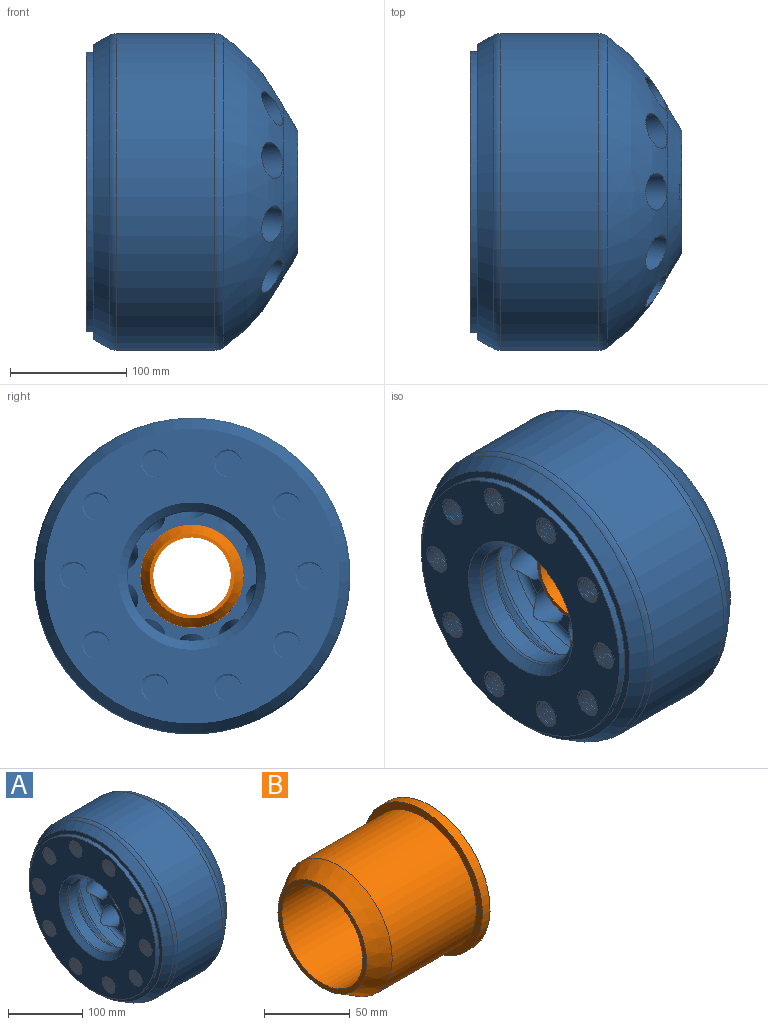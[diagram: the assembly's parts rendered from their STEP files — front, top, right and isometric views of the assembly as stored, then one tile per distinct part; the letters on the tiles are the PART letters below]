
ASSEMBLY  parts=2 mates=1
PART A: 256 faces, bbox 209.3x320.9x320.9 mm
  f0: cone r=52.39mm half-angle=59.3deg, axis (-1,0,0), area 9491.2mm2, adj f3,f15,f253,f254,f255
  f1: cylinder r=50.8mm len=101.6mm, axis (1,0,0), area 11189.3mm2, adj f2,f15,f253,f254
  f2: plane 114.3x114.3mm, normal (-1,0,0), area 2081.3mm2, adj f1,f23,f253,f254,f255
  f3: sphere r=165.1mm, area 45323.7mm2, adj f0,f16,f33,f34,f35,f36,f37,f38
  f4: cylinder r=79.38mm len=158.75mm, axis (1,0,0), area 6975.3mm2, adj f5,f6,f7,f8,f9,f10,f11,f12
  f5: torus R=73.03mm, axis (1,0,0), area 259.8mm2, adj f4,f26,f41,f42
  f6: torus R=73.03mm, axis (1,0,0), area 259.8mm2, adj f4,f26,f33,f42
  f7: torus R=73.03mm, axis (1,0,0), area 18306.5mm2, adj f4,f26,f40,f41
  f8: torus R=73.03mm, axis (1,0,0), area 0mm2, adj f4,f26,f39,f40
  f9: torus R=73.03mm, axis (1,0,0), area 494mm2, adj f4,f26,f38,f39
  f10: torus R=73.03mm, axis (1,0,0), area 259.8mm2, adj f4,f26,f37,f38
  f11: torus R=73.03mm, axis (1,0,0), area 259.8mm2, adj f4,f26,f36,f37
  f12: torus R=73.03mm, axis (1,0,0), area 18306.5mm2, adj f4,f26,f35,f36
  f13: torus R=73.03mm, axis (1,0,0), area 0mm2, adj f4,f26,f34,f35
  f14: torus R=73.03mm, axis (1,0,0), area 259.8mm2, adj f4,f26,f33,f34
  f15: plane 104.78x104.39mm, normal (1,0,0), area 494.4mm2, adj f0,f1,f253,f254
  f16: torus R=123.83mm, axis (-1,0,0), area 6740.3mm2, adj f3,f17
  f17: cylinder r=136.53mm len=273.05mm, axis (-1,0,0), area 72757.5mm2, adj f16,f18
  f18: torus R=123.83mm, axis (-1,0,0), area 5680.3mm2, adj f17,f19
  f19: cone r=127mm half-angle=30deg, axis (1,0,0), area 12870.4mm2, adj f18,f20
  f20: plane 254x254mm, normal (-1,0,0), area 4940.4mm2, adj f19,f21
  f21: cylinder r=120.65mm len=241.3mm, axis (-1,0,0), area 4813.7mm2, adj f20,f22
  f22: plane 242.26x242.26mm, normal (-1,0,0), area 28619.3mm2, adj f21,f32,f43,f44,f48,f61,f64,f65
  f23: cylinder r=57.15mm len=114.3mm, axis (1,0,0), area 2280.2mm2, adj f2,f24
  f24: plane 114.3x114.3mm, normal (1,0,0), area 4053.7mm2, adj f23,f25
  f25: cylinder r=44.45mm len=88.9mm, axis (1,0,0), area 18178.1mm2, adj f24,f26
  f26: plane 171.45x168.36mm, normal (-1,0,0), area 4413.4mm2, adj f5,f6,f7,f8,f9,f10,f11,f12
  f27: torus R=73.03mm, axis (1,0,0), area 2467.5mm2, adj f4,f28
  f28: cone r=56.49mm half-angle=45deg, axis (1,0,0), area 12516.5mm2, adj f27,f29
  f29: torus R=58.74mm, axis (1,0,0), area 875.5mm2, adj f28,f30
  f30: cylinder r=55.56mm len=111.13mm, axis (1,0,0), area 5732.3mm2, adj f29,f31
  f31: torus R=58.74mm, axis (1,0,0), area 875.5mm2, adj f30,f32
  f32: cone r=63.5mm half-angle=45deg, axis (-1,0,0), area 3735.8mm2, adj f22,f31
  f33: cylinder r=15.88mm len=105.94mm, axis (-0.97,0,-0.26), area 9094.1mm2, adj f3,f4,f6,f14,f26
  f34: cylinder r=15.88mm len=101.5mm, axis (-0.97,0.15,-0.21), area 8854.5mm2, adj f3,f4,f13,f14,f26
  f35: cylinder r=15.88mm len=105.94mm, axis (-0.97,0.25,-0.08), area 9081.9mm2, adj f3,f4,f12,f13,f26
  f36: cylinder r=15.88mm len=105.94mm, axis (-0.97,0.25,0.08), area 9082mm2, adj f3,f4,f11,f12,f26
  f37: cylinder r=15.88mm len=101.5mm, axis (-0.97,0.15,0.21), area 8835.7mm2, adj f3,f4,f10,f11,f26
  f38: cylinder r=15.88mm len=105.94mm, axis (-0.97,0,0.26), area 9106.3mm2, adj f3,f4,f9,f10,f26
  f39: cylinder r=15.88mm len=98.67mm, axis (-0.97,-0.15,0.21), area 8845.8mm2, adj f3,f4,f8,f9,f26
  f40: cylinder r=15.88mm len=105.94mm, axis (-0.97,-0.25,0.08), area 9052mm2, adj f3,f4,f7,f8,f26
  f41: cylinder r=15.88mm len=102.22mm, axis (-0.97,-0.25,-0.08), area 8973.2mm2, adj f3,f4,f5,f7,f26
  f42: cylinder r=15.88mm len=100.03mm, axis (-0.97,-0.15,-0.21), area 8769.5mm2, adj f3,f4,f5,f6,f26
  f43: bspline ~37.5x29.63mm, area 1693.9mm2, adj f22,f46,f48,f50,f51,f52,f53,f54
  f44: bspline ~36.45x29.63mm, area 1629.6mm2, adj f22,f45,f48,f51,f52,f53,f54,f55
  f45: bspline ~24.97x24.28mm, area 78.5mm2, adj f44,f47,f49,f50,f62
  f46: bspline ~24.86x24.06mm, area 78.4mm2, adj f43,f47,f49,f62
  f47: bspline ~25.26x24.57mm, area 35mm2, adj f45,f46,f48,f62
  f48: bspline ~36.38x29.97mm, area 413.9mm2, adj f22,f43,f44,f47
  f49: cylinder r=11.11mm len=22.23mm, axis (-1,0,0), area 1251.3mm2, adj f45,f46,f50,f62,f63
  f50: cylinder r=11.11mm len=22.23mm, axis (-1,0,0), area 87.5mm2, adj f43,f45,f49,f51
  f51: cylinder r=11.11mm len=22.23mm, axis (-1,0,0), area 55.5mm2, adj f43,f44,f50,f52
  f52: cylinder r=11.11mm len=22.23mm, axis (-1,0,0), area 55.5mm2, adj f43,f44,f51,f53
  f53: cylinder r=11.11mm len=22.23mm, axis (-1,0,0), area 55.4mm2, adj f43,f44,f52,f54
  f54: cylinder r=11.11mm len=22.23mm, axis (-1,0,0), area 55.4mm2, adj f43,f44,f53,f55
  f55: cylinder r=11.11mm len=22.23mm, axis (-1,0,0), area 55.3mm2, adj f43,f44,f54,f56
  f56: cylinder r=11.11mm len=22.23mm, axis (-1,0,0), area 55.4mm2, adj f43,f44,f55,f57
  f57: cylinder r=11.11mm len=22.23mm, axis (-1,0,0), area 55.5mm2, adj f43,f44,f56,f58
  f58: cylinder r=11.11mm len=22.23mm, axis (-1,0,0), area 55.4mm2, adj f43,f44,f57,f59
  f59: cylinder r=11.11mm len=22.23mm, axis (-1,0,0), area 55.5mm2, adj f43,f44,f58,f60
  f60: cylinder r=11.11mm len=22.23mm, axis (-1,0,0), area 55.4mm2, adj f43,f44,f59,f61
  f61: cylinder r=11.11mm len=22.23mm, axis (-1,0,0), area 34.6mm2, adj f22,f43,f44,f60
  f62: plane 0.56x0.24mm, normal (-0.01,1,0), area 0.1mm2, adj f45,f46,f47,f49
  f63: plane 22.23x22.23mm, normal (-1,0,0), area 387.9mm2, adj f49
  f64: bspline ~37.5x29.63mm, area 1693.9mm2, adj f22,f67,f69,f71,f72,f73,f74,f75
  f65: bspline ~36.45x29.63mm, area 1629.6mm2, adj f22,f66,f69,f72,f73,f74,f75,f76
  f66: bspline ~24.97x24.28mm, area 78.5mm2, adj f65,f68,f70,f71,f83
  f67: bspline ~24.97x24.28mm, area 78.4mm2, adj f64,f68,f70,f83
  f68: bspline ~25.26x24.57mm, area 35mm2, adj f66,f67,f69,f83
  f69: bspline ~36.38x29.97mm, area 413.9mm2, adj f22,f64,f65,f68
  f70: cylinder r=11.11mm len=22.23mm, axis (-1,0,0), area 1251.3mm2, adj f66,f67,f71,f83,f84
  f71: cylinder r=11.11mm len=22.23mm, axis (-1,0,0), area 87.5mm2, adj f64,f66,f70,f72
  f72: cylinder r=11.11mm len=22.23mm, axis (-1,0,0), area 55.5mm2, adj f64,f65,f71,f73
  f73: cylinder r=11.11mm len=22.23mm, axis (-1,0,0), area 55.5mm2, adj f64,f65,f72,f74
  f74: cylinder r=11.11mm len=22.23mm, axis (-1,0,0), area 55.4mm2, adj f64,f65,f73,f75
  f75: cylinder r=11.11mm len=22.23mm, axis (-1,0,0), area 55.4mm2, adj f64,f65,f74,f76
  f76: cylinder r=11.11mm len=22.23mm, axis (-1,0,0), area 55.3mm2, adj f64,f65,f75,f77
  f77: cylinder r=11.11mm len=22.23mm, axis (-1,0,0), area 55.4mm2, adj f64,f65,f76,f78
  f78: cylinder r=11.11mm len=22.23mm, axis (-1,0,0), area 55.5mm2, adj f64,f65,f77,f79
  f79: cylinder r=11.11mm len=22.23mm, axis (-1,0,0), area 55.4mm2, adj f64,f65,f78,f80
  f80: cylinder r=11.11mm len=22.23mm, axis (-1,0,0), area 55.5mm2, adj f64,f65,f79,f81
  f81: cylinder r=11.11mm len=22.23mm, axis (-1,0,0), area 55.4mm2, adj f64,f65,f80,f82
  f82: cylinder r=11.11mm len=22.23mm, axis (-1,0,0), area 34.6mm2, adj f22,f64,f65,f81
  f83: plane 0.56x0.24mm, normal (-0.01,1,0), area 0.1mm2, adj f66,f67,f68,f70
  f84: plane 22.23x22.23mm, normal (-1,0,0), area 387.9mm2, adj f70
  f85: bspline ~37.5x29.63mm, area 1693.9mm2, adj f22,f88,f90,f92,f93,f94,f95,f96
  f86: bspline ~36.45x29.63mm, area 1629.6mm2, adj f22,f87,f90,f93,f94,f95,f96,f97
  f87: bspline ~24.97x24.28mm, area 78.5mm2, adj f86,f89,f91,f92,f104
  f88: bspline ~24.97x24.28mm, area 78.4mm2, adj f85,f89,f91,f104
  f89: bspline ~25.26x24.57mm, area 35mm2, adj f87,f88,f90,f104
  f90: bspline ~36.38x29.97mm, area 413.9mm2, adj f22,f85,f86,f89
  f91: cylinder r=11.11mm len=22.23mm, axis (-1,0,0), area 1251.3mm2, adj f87,f88,f92,f104,f105
  f92: cylinder r=11.11mm len=22.23mm, axis (-1,0,0), area 87.5mm2, adj f85,f87,f91,f93
  f93: cylinder r=11.11mm len=22.23mm, axis (-1,0,0), area 55.5mm2, adj f85,f86,f92,f94
  f94: cylinder r=11.11mm len=22.23mm, axis (-1,0,0), area 55.5mm2, adj f85,f86,f93,f95
  f95: cylinder r=11.11mm len=22.23mm, axis (-1,0,0), area 55.4mm2, adj f85,f86,f94,f96
  f96: cylinder r=11.11mm len=22.23mm, axis (-1,0,0), area 55.4mm2, adj f85,f86,f95,f97
  f97: cylinder r=11.11mm len=22.23mm, axis (-1,0,0), area 55.3mm2, adj f85,f86,f96,f98
  f98: cylinder r=11.11mm len=22.23mm, axis (-1,0,0), area 55.4mm2, adj f85,f86,f97,f99
  f99: cylinder r=11.11mm len=22.23mm, axis (-1,0,0), area 55.5mm2, adj f85,f86,f98,f100
  f100: cylinder r=11.11mm len=22.23mm, axis (-1,0,0), area 55.4mm2, adj f85,f86,f99,f101
  f101: cylinder r=11.11mm len=22.23mm, axis (-1,0,0), area 55.5mm2, adj f85,f86,f100,f102
  f102: cylinder r=11.11mm len=22.23mm, axis (-1,0,0), area 55.4mm2, adj f85,f86,f101,f103
  f103: cylinder r=11.11mm len=22.23mm, axis (-1,0,0), area 34.6mm2, adj f22,f85,f86,f102
  f104: plane 0.56x0.24mm, normal (-0.01,1,0), area 0.1mm2, adj f87,f88,f89,f91
  f105: plane 22.23x22.23mm, normal (-1,0,0), area 387.9mm2, adj f91
  f106: bspline ~37.5x29.63mm, area 1693.9mm2, adj f22,f109,f111,f113,f114,f115,f116,f117
  f107: bspline ~36.45x29.63mm, area 1629.6mm2, adj f22,f108,f111,f114,f115,f116,f117,f118
  f108: bspline ~24.86x24.06mm, area 78.5mm2, adj f107,f110,f112,f113,f125
  f109: bspline ~24.97x24.28mm, area 78.4mm2, adj f106,f110,f112,f125
  f110: bspline ~25.26x24.57mm, area 35mm2, adj f108,f109,f111,f125
  f111: bspline ~36.38x29.97mm, area 413.9mm2, adj f22,f106,f107,f110
  f112: cylinder r=11.11mm len=22.23mm, axis (-1,0,0), area 1251.3mm2, adj f108,f109,f113,f125,f126
  f113: cylinder r=11.11mm len=22.23mm, axis (-1,0,0), area 87.5mm2, adj f106,f108,f112,f114
  f114: cylinder r=11.11mm len=22.23mm, axis (-1,0,0), area 55.5mm2, adj f106,f107,f113,f115
  f115: cylinder r=11.11mm len=22.23mm, axis (-1,0,0), area 55.5mm2, adj f106,f107,f114,f116
  f116: cylinder r=11.11mm len=22.23mm, axis (-1,0,0), area 55.4mm2, adj f106,f107,f115,f117
  f117: cylinder r=11.11mm len=22.23mm, axis (-1,0,0), area 55.4mm2, adj f106,f107,f116,f118
  f118: cylinder r=11.11mm len=22.23mm, axis (-1,0,0), area 55.3mm2, adj f106,f107,f117,f119
  f119: cylinder r=11.11mm len=22.23mm, axis (-1,0,0), area 55.4mm2, adj f106,f107,f118,f120
  f120: cylinder r=11.11mm len=22.23mm, axis (-1,0,0), area 55.5mm2, adj f106,f107,f119,f121
  f121: cylinder r=11.11mm len=22.23mm, axis (-1,0,0), area 55.4mm2, adj f106,f107,f120,f122
  f122: cylinder r=11.11mm len=22.23mm, axis (-1,0,0), area 55.5mm2, adj f106,f107,f121,f123
  f123: cylinder r=11.11mm len=22.23mm, axis (-1,0,0), area 55.4mm2, adj f106,f107,f122,f124
  f124: cylinder r=11.11mm len=22.23mm, axis (-1,0,0), area 34.6mm2, adj f22,f106,f107,f123
  f125: plane 0.56x0.24mm, normal (-0.01,1,0), area 0.1mm2, adj f108,f109,f110,f112
  f126: plane 22.23x22.23mm, normal (-1,0,0), area 387.9mm2, adj f112
  f127: bspline ~37.5x29.63mm, area 1693.9mm2, adj f22,f130,f132,f134,f135,f136,f137,f138
  f128: bspline ~36.45x29.63mm, area 1629.6mm2, adj f22,f129,f132,f135,f136,f137,f138,f139
  f129: bspline ~24.86x24.06mm, area 78.5mm2, adj f128,f131,f133,f134,f146
  f130: bspline ~24.97x24.28mm, area 78.4mm2, adj f127,f131,f133,f146
  f131: bspline ~25.26x24.57mm, area 35mm2, adj f129,f130,f132,f146
  f132: bspline ~36.38x29.97mm, area 413.9mm2, adj f22,f127,f128,f131
  f133: cylinder r=11.11mm len=22.23mm, axis (-1,0,0), area 1251.3mm2, adj f129,f130,f134,f146,f147
  f134: cylinder r=11.11mm len=22.23mm, axis (-1,0,0), area 87.5mm2, adj f127,f129,f133,f135
  f135: cylinder r=11.11mm len=22.23mm, axis (-1,0,0), area 55.5mm2, adj f127,f128,f134,f136
  f136: cylinder r=11.11mm len=22.23mm, axis (-1,0,0), area 55.5mm2, adj f127,f128,f135,f137
  f137: cylinder r=11.11mm len=22.23mm, axis (-1,0,0), area 55.4mm2, adj f127,f128,f136,f138
  f138: cylinder r=11.11mm len=22.23mm, axis (-1,0,0), area 55.4mm2, adj f127,f128,f137,f139
  f139: cylinder r=11.11mm len=22.23mm, axis (-1,0,0), area 55.3mm2, adj f127,f128,f138,f140
  f140: cylinder r=11.11mm len=22.23mm, axis (-1,0,0), area 55.4mm2, adj f127,f128,f139,f141
  f141: cylinder r=11.11mm len=22.23mm, axis (-1,0,0), area 55.5mm2, adj f127,f128,f140,f142
  f142: cylinder r=11.11mm len=22.23mm, axis (-1,0,0), area 55.4mm2, adj f127,f128,f141,f143
  f143: cylinder r=11.11mm len=22.23mm, axis (-1,0,0), area 55.5mm2, adj f127,f128,f142,f144
  f144: cylinder r=11.11mm len=22.23mm, axis (-1,0,0), area 55.4mm2, adj f127,f128,f143,f145
  f145: cylinder r=11.11mm len=22.23mm, axis (-1,0,0), area 34.6mm2, adj f22,f127,f128,f144
  f146: plane 0.56x0.24mm, normal (-0.01,1,0), area 0.1mm2, adj f129,f130,f131,f133
  f147: plane 22.23x22.23mm, normal (-1,0,0), area 387.9mm2, adj f133
  f148: bspline ~37.5x29.63mm, area 1693.9mm2, adj f22,f151,f153,f155,f156,f157,f158,f159
  f149: bspline ~36.45x29.63mm, area 1629.6mm2, adj f22,f150,f153,f156,f157,f158,f159,f160
  f150: bspline ~24.97x24.28mm, area 78.5mm2, adj f149,f152,f154,f155,f167
  f151: bspline ~24.86x24.06mm, area 78.4mm2, adj f148,f152,f154,f167
  f152: bspline ~25.26x24.57mm, area 35mm2, adj f150,f151,f153,f167
  f153: bspline ~36.38x29.97mm, area 413.9mm2, adj f22,f148,f149,f152
  f154: cylinder r=11.11mm len=22.23mm, axis (-1,0,0), area 1251.3mm2, adj f150,f151,f155,f167,f168
  f155: cylinder r=11.11mm len=22.23mm, axis (-1,0,0), area 87.5mm2, adj f148,f150,f154,f156
  f156: cylinder r=11.11mm len=22.23mm, axis (-1,0,0), area 55.5mm2, adj f148,f149,f155,f157
  f157: cylinder r=11.11mm len=22.23mm, axis (-1,0,0), area 55.5mm2, adj f148,f149,f156,f158
  f158: cylinder r=11.11mm len=22.23mm, axis (-1,0,0), area 55.4mm2, adj f148,f149,f157,f159
  f159: cylinder r=11.11mm len=22.23mm, axis (-1,0,0), area 55.4mm2, adj f148,f149,f158,f160
  f160: cylinder r=11.11mm len=22.23mm, axis (-1,0,0), area 55.3mm2, adj f148,f149,f159,f161
  f161: cylinder r=11.11mm len=22.23mm, axis (-1,0,0), area 55.4mm2, adj f148,f149,f160,f162
  f162: cylinder r=11.11mm len=22.23mm, axis (-1,0,0), area 55.5mm2, adj f148,f149,f161,f163
  f163: cylinder r=11.11mm len=22.23mm, axis (-1,0,0), area 55.4mm2, adj f148,f149,f162,f164
  f164: cylinder r=11.11mm len=22.23mm, axis (-1,0,0), area 55.5mm2, adj f148,f149,f163,f165
  f165: cylinder r=11.11mm len=22.23mm, axis (-1,0,0), area 55.4mm2, adj f148,f149,f164,f166
  f166: cylinder r=11.11mm len=22.23mm, axis (-1,0,0), area 34.6mm2, adj f22,f148,f149,f165
  f167: plane 0.56x0.24mm, normal (-0.01,1,0), area 0.1mm2, adj f150,f151,f152,f154
  f168: plane 22.23x22.23mm, normal (-1,0,0), area 387.9mm2, adj f154
  f169: bspline ~37.5x29.63mm, area 1693.9mm2, adj f22,f172,f174,f176,f177,f178,f179,f180
  f170: bspline ~36.45x29.63mm, area 1629.6mm2, adj f22,f171,f174,f177,f178,f179,f180,f181
  f171: bspline ~24.86x24.06mm, area 78.5mm2, adj f170,f173,f175,f176,f188
  f172: bspline ~24.97x24.28mm, area 78.4mm2, adj f169,f173,f175,f188
  f173: bspline ~25.26x24.57mm, area 35mm2, adj f171,f172,f174,f188
  f174: bspline ~36.38x29.97mm, area 413.9mm2, adj f22,f169,f170,f173
  f175: cylinder r=11.11mm len=22.23mm, axis (-1,0,0), area 1251.3mm2, adj f171,f172,f176,f188,f189
  f176: cylinder r=11.11mm len=22.23mm, axis (-1,0,0), area 87.5mm2, adj f169,f171,f175,f177
  f177: cylinder r=11.11mm len=22.23mm, axis (-1,0,0), area 55.5mm2, adj f169,f170,f176,f178
  f178: cylinder r=11.11mm len=22.23mm, axis (-1,0,0), area 55.5mm2, adj f169,f170,f177,f179
  f179: cylinder r=11.11mm len=22.23mm, axis (-1,0,0), area 55.4mm2, adj f169,f170,f178,f180
  f180: cylinder r=11.11mm len=22.23mm, axis (-1,0,0), area 55.4mm2, adj f169,f170,f179,f181
  f181: cylinder r=11.11mm len=22.23mm, axis (-1,0,0), area 55.3mm2, adj f169,f170,f180,f182
  f182: cylinder r=11.11mm len=22.23mm, axis (-1,0,0), area 55.4mm2, adj f169,f170,f181,f183
  f183: cylinder r=11.11mm len=22.23mm, axis (-1,0,0), area 55.5mm2, adj f169,f170,f182,f184
  f184: cylinder r=11.11mm len=22.23mm, axis (-1,0,0), area 55.4mm2, adj f169,f170,f183,f185
  f185: cylinder r=11.11mm len=22.23mm, axis (-1,0,0), area 55.5mm2, adj f169,f170,f184,f186
  f186: cylinder r=11.11mm len=22.23mm, axis (-1,0,0), area 55.4mm2, adj f169,f170,f185,f187
  f187: cylinder r=11.11mm len=22.23mm, axis (-1,0,0), area 34.6mm2, adj f22,f169,f170,f186
  f188: plane 0.56x0.24mm, normal (-0.01,1,0), area 0.1mm2, adj f171,f172,f173,f175
  f189: plane 22.23x22.23mm, normal (-1,0,0), area 387.9mm2, adj f175
  f190: bspline ~37.5x29.63mm, area 1693.9mm2, adj f22,f193,f195,f197,f198,f199,f200,f201
  f191: bspline ~36.45x29.63mm, area 1629.6mm2, adj f22,f192,f195,f198,f199,f200,f201,f202
  f192: bspline ~24.86x24.06mm, area 78.5mm2, adj f191,f194,f196,f197,f209
  f193: bspline ~24.97x24.28mm, area 78.4mm2, adj f190,f194,f196,f209
  f194: bspline ~25.26x24.57mm, area 35mm2, adj f192,f193,f195,f209
  f195: bspline ~36.38x29.97mm, area 413.9mm2, adj f22,f190,f191,f194
  f196: cylinder r=11.11mm len=22.23mm, axis (-1,0,0), area 1251.3mm2, adj f192,f193,f197,f209,f210
  f197: cylinder r=11.11mm len=22.23mm, axis (-1,0,0), area 87.5mm2, adj f190,f192,f196,f198
  f198: cylinder r=11.11mm len=22.23mm, axis (-1,0,0), area 55.5mm2, adj f190,f191,f197,f199
  f199: cylinder r=11.11mm len=22.23mm, axis (-1,0,0), area 55.5mm2, adj f190,f191,f198,f200
  f200: cylinder r=11.11mm len=22.23mm, axis (-1,0,0), area 55.4mm2, adj f190,f191,f199,f201
  f201: cylinder r=11.11mm len=22.23mm, axis (-1,0,0), area 55.4mm2, adj f190,f191,f200,f202
  f202: cylinder r=11.11mm len=22.23mm, axis (-1,0,0), area 55.3mm2, adj f190,f191,f201,f203
  f203: cylinder r=11.11mm len=22.23mm, axis (-1,0,0), area 55.4mm2, adj f190,f191,f202,f204
  f204: cylinder r=11.11mm len=22.23mm, axis (-1,0,0), area 55.5mm2, adj f190,f191,f203,f205
  f205: cylinder r=11.11mm len=22.23mm, axis (-1,0,0), area 55.4mm2, adj f190,f191,f204,f206
  f206: cylinder r=11.11mm len=22.23mm, axis (-1,0,0), area 55.5mm2, adj f190,f191,f205,f207
  f207: cylinder r=11.11mm len=22.23mm, axis (-1,0,0), area 55.4mm2, adj f190,f191,f206,f208
  f208: cylinder r=11.11mm len=22.23mm, axis (-1,0,0), area 34.6mm2, adj f22,f190,f191,f207
  f209: plane 0.56x0.24mm, normal (-0.01,1,0), area 0.1mm2, adj f192,f193,f194,f196
  f210: plane 22.23x22.23mm, normal (-1,0,0), area 387.9mm2, adj f196
  f211: bspline ~37.5x29.63mm, area 1693.9mm2, adj f22,f214,f216,f218,f219,f220,f221,f222
  f212: bspline ~36.45x29.63mm, area 1629.6mm2, adj f22,f213,f216,f219,f220,f221,f222,f223
  f213: bspline ~24.97x24.28mm, area 78.5mm2, adj f212,f215,f217,f218,f230
  f214: bspline ~24.97x24.28mm, area 78.4mm2, adj f211,f215,f217,f230
  f215: bspline ~25.26x24.57mm, area 35mm2, adj f213,f214,f216,f230
  f216: bspline ~36.38x29.97mm, area 413.9mm2, adj f22,f211,f212,f215
  f217: cylinder r=11.11mm len=22.23mm, axis (-1,0,0), area 1251.3mm2, adj f213,f214,f218,f230,f231
  f218: cylinder r=11.11mm len=22.23mm, axis (-1,0,0), area 87.5mm2, adj f211,f213,f217,f219
  f219: cylinder r=11.11mm len=22.23mm, axis (-1,0,0), area 55.5mm2, adj f211,f212,f218,f220
  f220: cylinder r=11.11mm len=22.23mm, axis (-1,0,0), area 55.5mm2, adj f211,f212,f219,f221
  f221: cylinder r=11.11mm len=22.23mm, axis (-1,0,0), area 55.4mm2, adj f211,f212,f220,f222
  f222: cylinder r=11.11mm len=22.23mm, axis (-1,0,0), area 55.4mm2, adj f211,f212,f221,f223
  f223: cylinder r=11.11mm len=22.23mm, axis (-1,0,0), area 55.3mm2, adj f211,f212,f222,f224
  f224: cylinder r=11.11mm len=22.23mm, axis (-1,0,0), area 55.4mm2, adj f211,f212,f223,f225
  f225: cylinder r=11.11mm len=22.23mm, axis (-1,0,0), area 55.5mm2, adj f211,f212,f224,f226
  f226: cylinder r=11.11mm len=22.23mm, axis (-1,0,0), area 55.4mm2, adj f211,f212,f225,f227
  f227: cylinder r=11.11mm len=22.23mm, axis (-1,0,0), area 55.5mm2, adj f211,f212,f226,f228
  f228: cylinder r=11.11mm len=22.23mm, axis (-1,0,0), area 55.4mm2, adj f211,f212,f227,f229
  f229: cylinder r=11.11mm len=22.23mm, axis (-1,0,0), area 34.6mm2, adj f22,f211,f212,f228
  f230: plane 0.56x0.24mm, normal (-0.01,1,0), area 0.1mm2, adj f213,f214,f215,f217
  f231: plane 22.23x22.23mm, normal (-1,0,0), area 387.9mm2, adj f217
  f232: bspline ~37.5x29.63mm, area 1693.9mm2, adj f22,f235,f237,f239,f240,f241,f242,f243
  f233: bspline ~36.45x29.63mm, area 1629.6mm2, adj f22,f234,f237,f240,f241,f242,f243,f244
  f234: bspline ~24.97x24.28mm, area 78.5mm2, adj f233,f236,f238,f239,f251
  f235: bspline ~24.97x24.28mm, area 78.4mm2, adj f232,f236,f238,f251
  f236: bspline ~25.26x24.57mm, area 35mm2, adj f234,f235,f237,f251
  f237: bspline ~36.38x29.97mm, area 413.9mm2, adj f22,f232,f233,f236
  f238: cylinder r=11.11mm len=22.23mm, axis (-1,0,0), area 1251.3mm2, adj f234,f235,f239,f251,f252
  f239: cylinder r=11.11mm len=22.23mm, axis (-1,0,0), area 87.5mm2, adj f232,f234,f238,f240
  f240: cylinder r=11.11mm len=22.23mm, axis (-1,0,0), area 55.5mm2, adj f232,f233,f239,f241
  f241: cylinder r=11.11mm len=22.23mm, axis (-1,0,0), area 55.5mm2, adj f232,f233,f240,f242
  f242: cylinder r=11.11mm len=22.23mm, axis (-1,0,0), area 55.4mm2, adj f232,f233,f241,f243
  f243: cylinder r=11.11mm len=22.23mm, axis (-1,0,0), area 55.4mm2, adj f232,f233,f242,f244
  f244: cylinder r=11.11mm len=22.23mm, axis (-1,0,0), area 55.3mm2, adj f232,f233,f243,f245
  f245: cylinder r=11.11mm len=22.23mm, axis (-1,0,0), area 55.4mm2, adj f232,f233,f244,f246
  f246: cylinder r=11.11mm len=22.23mm, axis (-1,0,0), area 55.5mm2, adj f232,f233,f245,f247
  f247: cylinder r=11.11mm len=22.23mm, axis (-1,0,0), area 55.4mm2, adj f232,f233,f246,f248
  f248: cylinder r=11.11mm len=22.23mm, axis (-1,0,0), area 55.5mm2, adj f232,f233,f247,f249
  f249: cylinder r=11.11mm len=22.23mm, axis (-1,0,0), area 55.4mm2, adj f232,f233,f248,f250
  f250: cylinder r=11.11mm len=22.23mm, axis (-1,0,0), area 34.6mm2, adj f22,f232,f233,f249
  f251: plane 0.56x0.24mm, normal (-0.01,1,0), area 0.1mm2, adj f234,f235,f236,f238
  f252: plane 22.23x22.23mm, normal (-1,0,0), area 387.9mm2, adj f238
  f253: plane 36.53x5.97mm, normal (0,1,0), area 211.8mm2, adj f0,f1,f2,f15,f255
  f254: plane 36.53x5.97mm, normal (0,-1,0), area 211.8mm2, adj f0,f1,f2,f15,f255
  f255: plane 34.37x12.91mm, normal (0,0,-1), area 432.9mm2, adj f0,f2,f253,f254
PART B: 8 faces, bbox 88.9x98.4x98.4 mm
  f0: plane 73.03x73.03mm, normal (-1,0,0), area 696.7mm2, adj f1,f6
  f1: cylinder r=33.34mm len=87.31mm, axis (-1,0,0), area 18289mm2, adj f0,f7
  f2: plane 98.43x98.43mm, normal (1,0,0), area 3776.6mm2, adj f3,f7
  f3: cylinder r=49.21mm len=98.43mm, axis (-1,0,0), area 1963.5mm2, adj f2,f4
  f4: plane 98.43x98.43mm, normal (-1,0,0), area 1472.1mm2, adj f3,f5
  f5: cylinder r=44.2mm len=88.39mm, axis (-1,0,0), area 19227.9mm2, adj f4,f6
  f6: cone r=44.2mm half-angle=30deg, axis (1,0,0), area 3896.4mm2, adj f0,f5
  f7: cone r=34.92mm half-angle=45deg, axis (1,0,0), area 481.5mm2, adj f1,f2
PLACE A t=(80.53,4.27,-0.27)mm
PLACE B t=(137.68,4.27,-0.27)mm
MATE planar A.f23 <-> B.f1  axis (1,0,0) through (220.23,4.27,-0.27)mm
